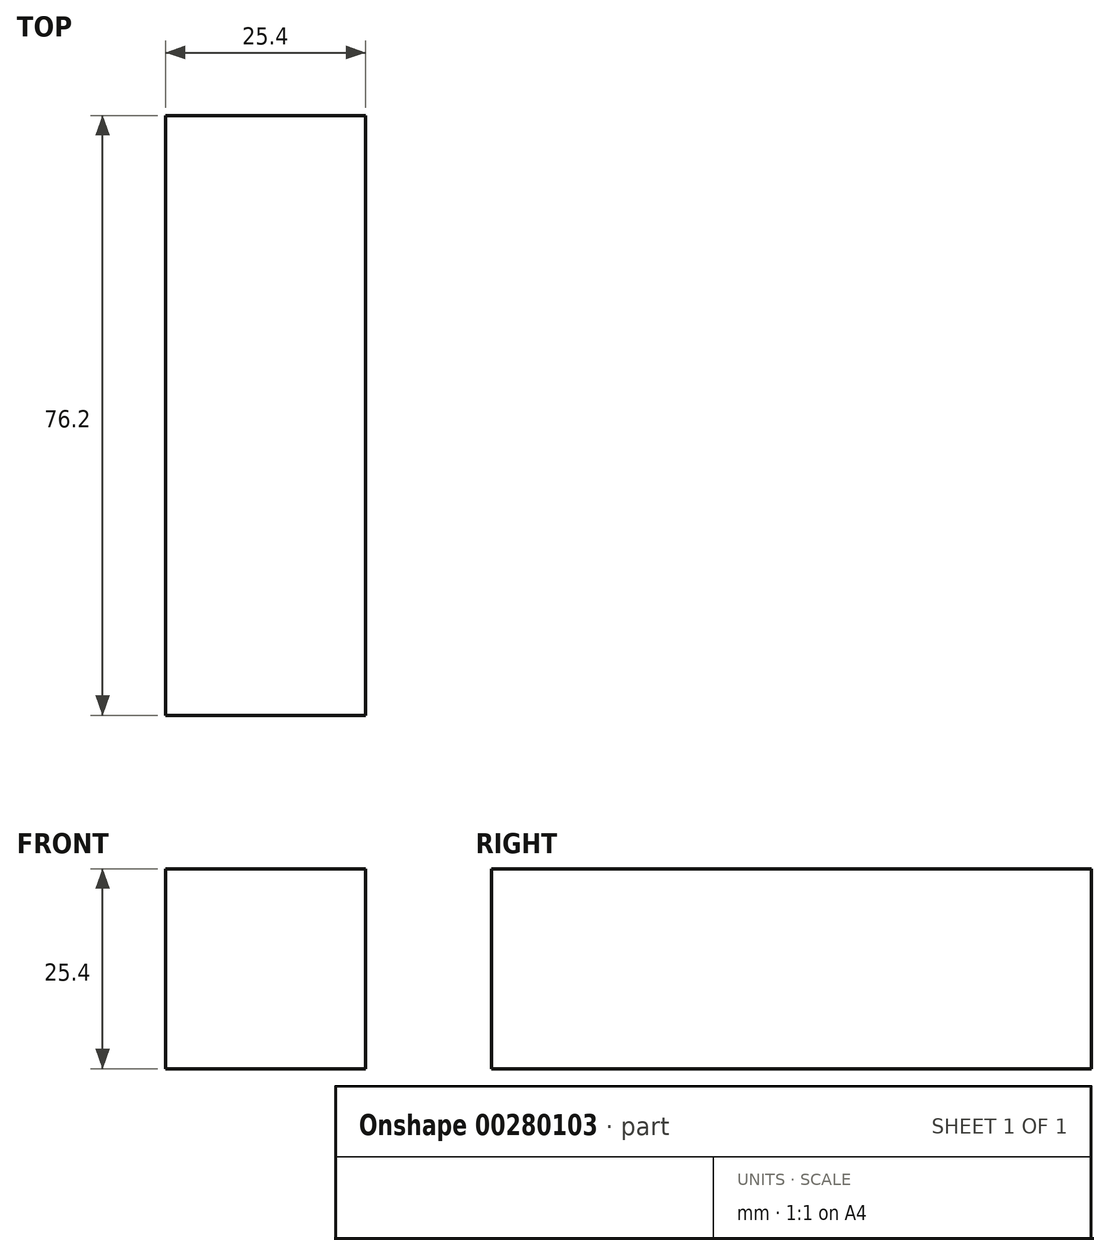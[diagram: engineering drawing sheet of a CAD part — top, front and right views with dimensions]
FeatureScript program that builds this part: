
annotation { "Feature Type Name" : "Feature", "Feature Type Description" : "" }
export const myFeature = defineFeature(function(context is Context, id is Id, definition is map)
    precondition{}
    {
        {
            var Q0;
            Q0=qCreatedBy(makeId("Front.planeOp"),FACE);
            var sketch = newSketch(context, id + "F0", { "sketchPlane" : qUnion([Q0])});
            skLineSegment(sketch, "E0.bottom", {"start": v(-43.54, 33.04) * mm, "end": v(-18.14, 33.04) * mm});
            skLineSegment(sketch, "E0.top", {"start": v(-43.54, 7.64) * mm, "end": v(-18.14, 7.64) * mm});
            skLineSegment(sketch, "E0.left", {"start": v(-43.54, 33.04) * mm, "end": v(-43.54, 7.64) * mm});
            skLineSegment(sketch, "E0.right", {"start": v(-18.14, 33.04) * mm, "end": v(-18.14, 7.64) * mm});
            skSolve(sketch);
        }
        {
            var Q0;
            Q0 = qSketchRegion(id + "F0", true);
            extrude(context, id + "F1", {"entities" : qUnion([Q0]), "depth" : 76.2 * mm});
        }
    });
